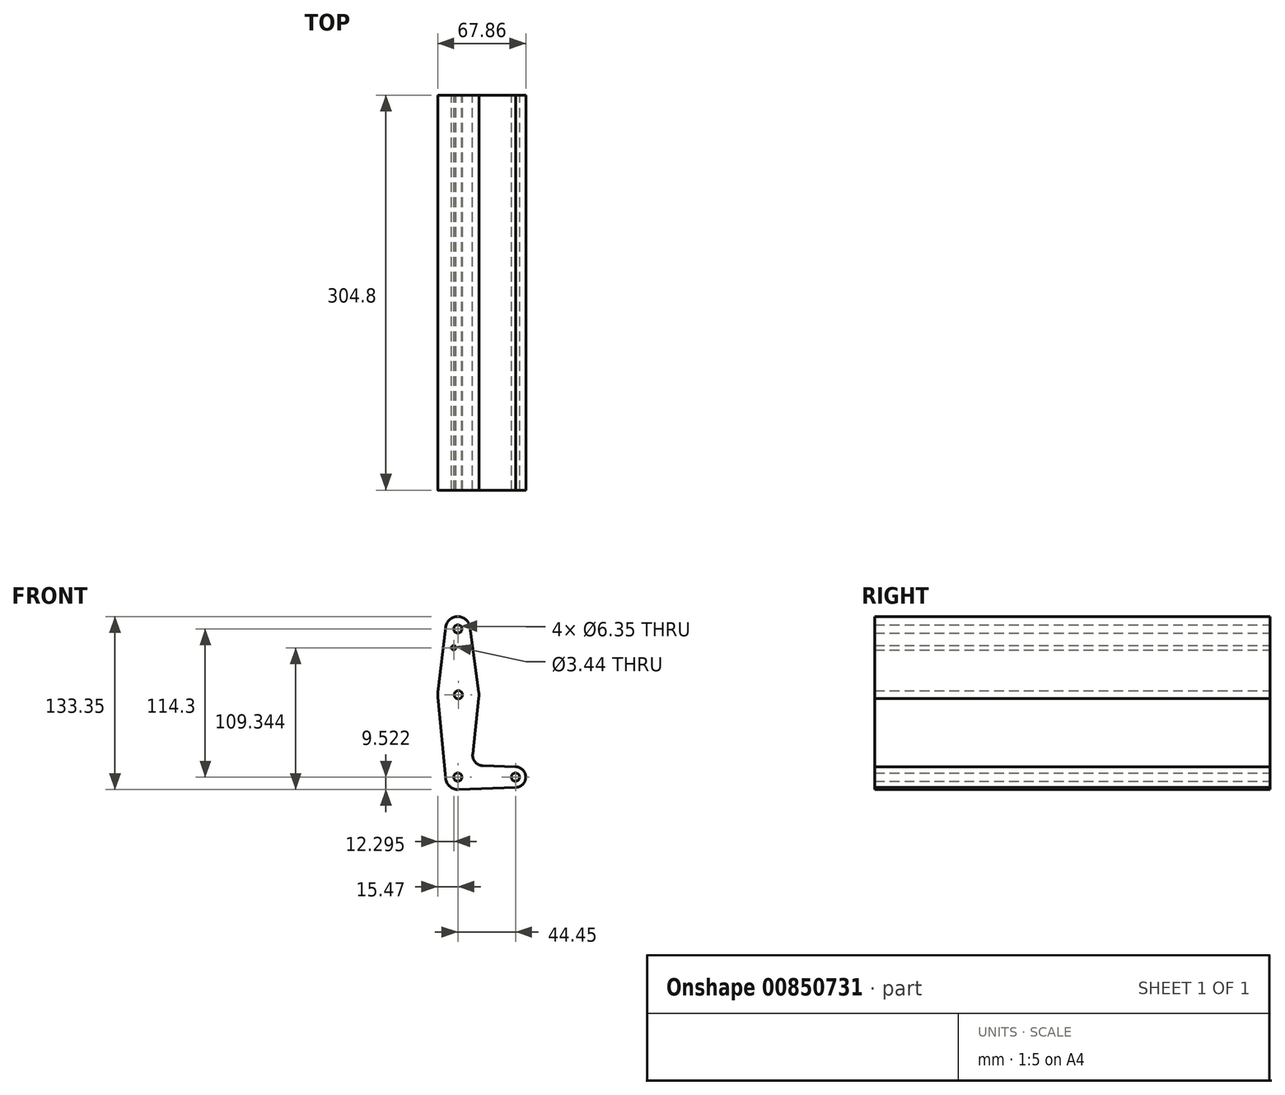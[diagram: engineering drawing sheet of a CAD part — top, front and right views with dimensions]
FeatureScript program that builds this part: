
annotation { "Feature Type Name" : "Feature", "Feature Type Description" : "" }
export const myFeature = defineFeature(function(context is Context, id is Id, definition is map)
    precondition{}
    {
        {
            var Q0;
            Q0=qCreatedBy(makeId("Front.planeOp"),FACE);
            var sketch = newSketch(context, id + "F0", { "sketchPlane" : qUnion([Q0])});
            skCircle(sketch, "E0", {"center": v(-44.45, 103.47) * mm, "radius": 9.53 * mm});
            skCircle(sketch, "E1", {"center": v(-44.05, 52.67) * mm, "radius": 15.88 * mm});
            skCircle(sketch, "E2", {"center": v(-44.45, -10.83) * mm, "radius": 9.53 * mm});
            skCircle(sketch, "E3", {"center": v(0, -10.83) * mm, "radius": 7.94 * mm});
            skLineSegment(sketch, "E4", {"start": v(-44.45, 103.47) * mm, "end": v(-44.45, -10.83) * mm});
            skLineSegment(sketch, "E5", {"start": v(-59.85, 51.18) * mm, "end": v(-53.93, -11.72) * mm});
            skLineSegment(sketch, "E6", {"start": v(-53.9, 104.59) * mm, "end": v(-59.82, 54.53) * mm});
            skLineSegment(sketch, "E7", {"start": v(-35, 104.74) * mm, "end": v(-28.32, 54.78) * mm});
            skCircle(sketch, "E8", {"center": v(-44.45, -10.83) * mm, "radius": 3.18 * mm});
            skCircle(sketch, "E9", {"center": v(-44.05, 52.67) * mm, "radius": 3.18 * mm});
            skCircle(sketch, "E10", {"center": v(-44.45, 103.47) * mm, "radius": 3.18 * mm});
            skCircle(sketch, "E11", {"center": v(0, -10.83) * mm, "radius": 3.18 * mm});
            skCircle(sketch, "E12", {"center": v(-47.63, 89) * mm, "radius": 1.72 * mm});
            skLineSegment(sketch, "E13", {"start": v(-28.41, 49.95) * mm, "end": v(-33, 6.8) * mm});
            skLineSegment(sketch, "E14", {"start": v(0, -10.83) * mm, "end": v(-44.45, -10.83) * mm});
            skLineSegment(sketch, "E15", {"start": v(0, -2.9) * mm, "end": v(-25.38, -1.98) * mm});
            skLineSegment(sketch, "E16", {"start": v(0, -18.77) * mm, "end": v(-44.1, -20.35) * mm});
            skArc(sketch, "E17.filletArc", {"start": v(-33, 6.8) * mm, "mid": v(-31.1, 0.75) * mm, "end": v(-25.38, -1.98) * mm});
            skSolve(sketch);
        }
        {
            var Q0;
            {var subQ10=sQuery(id+"F0.wireOp",EDGE,"E13");Q0=makeQuery(id+"F0.imprint","IMPRINT",FACE,{"disambiguationData":[TD([[makeQuery(id+"F0.imprint","IMPRINT",EDGE,{"derivedFrom":subQ10}),-1.0]])]});}
            var Q1;
            {var subQ0=sQuery(id+"F0.wireOp",EDGE,"E5");Q1=makeQuery(id+"F0.imprint","IMPRINT",FACE,{"disambiguationData":[TD([[makeQuery(id+"F0.imprint","IMPRINT",EDGE,{"derivedFrom":subQ0}),1.0]])]});}
            var Q2;
            {var subQ0=sQuery(id+"F0.wireOp",EDGE,"E2");var subQ8=makeQuery(id+"F0.imprint","INTERSECT",VERTEX,{"derivedFrom":[subQ0,sQuery(id+"F0.wireOp",EDGE,"E5")]});Q2=makeQuery(id+"F0.imprint","IMPRINT",FACE,{"disambiguationData":[TD([[makeQuery(id+"F0.imprint","IMPRINT",EDGE,{"disambiguationData":[TD([[subQ8,1.0]])],"derivedFrom":subQ0}),1.0]])]});}
            var Q3;
            {var subQ0=sQuery(id+"F0.wireOp",EDGE,"E4");var subQ1=sQuery(id+"F0.wireOp",EDGE,"E2");var subQ2=makeQuery(id+"F0.imprint","INTERSECT",VERTEX,{"derivedFrom":[subQ1,subQ0]});Q3=makeQuery(id+"F0.imprint","IMPRINT",FACE,{"disambiguationData":[TD([[makeQuery(id+"F0.imprint","IMPRINT",EDGE,{"disambiguationData":[TD([[subQ2,1.0]])],"derivedFrom":subQ1}),1.0]])]});}
            var Q4;
            {var subQ0=sQuery(id+"F0.wireOp",EDGE,"E16");Q4=makeQuery(id+"F0.imprint","IMPRINT",FACE,{"disambiguationData":[TD([[makeQuery(id+"F0.imprint","IMPRINT",EDGE,{"derivedFrom":subQ0}),-1.0]])]});}
            var Q5;
            Q5=makeQuery(id+"F0.imprint","IMPRINT",FACE,{"disambiguationData":[TD([[makeQuery(id+"F0.imprint","IMPRINT",EDGE,{"derivedFrom":sQuery(id+"F0.wireOp",EDGE,"E11")}),-1.0]])]});
            var Q6;
            {var subQ1=sQuery(id+"F0.wireOp",EDGE,"E1");var subQ8=makeQuery(id+"F0.imprint","INTERSECT",VERTEX,{"derivedFrom":[subQ1,sQuery(id+"F0.wireOp",EDGE,"E7")]});Q6=makeQuery(id+"F0.imprint","IMPRINT",FACE,{"disambiguationData":[TD([[makeQuery(id+"F0.imprint","IMPRINT",EDGE,{"disambiguationData":[TD([[subQ8,-1.0]])],"derivedFrom":subQ1}),1.0]])]});}
            var Q7;
            {var subQ1=sQuery(id+"F0.wireOp",EDGE,"E1");var subQ8=makeQuery(id+"F0.imprint","INTERSECT",VERTEX,{"derivedFrom":[subQ1,sQuery(id+"F0.wireOp",EDGE,"E6")]});Q7=makeQuery(id+"F0.imprint","IMPRINT",FACE,{"disambiguationData":[TD([[makeQuery(id+"F0.imprint","IMPRINT",EDGE,{"disambiguationData":[TD([[subQ8,1.0]])],"derivedFrom":subQ1}),1.0]])]});}
            var Q8;
            {var subQ0=sQuery(id+"F0.wireOp",EDGE,"E6");Q8=makeQuery(id+"F0.imprint","IMPRINT",FACE,{"disambiguationData":[TD([[makeQuery(id+"F0.imprint","IMPRINT",EDGE,{"derivedFrom":subQ0}),1.0]])]});}
            var Q9;
            {var subQ0=sQuery(id+"F0.wireOp",EDGE,"E7");Q9=makeQuery(id+"F0.imprint","IMPRINT",FACE,{"disambiguationData":[TD([[makeQuery(id+"F0.imprint","IMPRINT",EDGE,{"derivedFrom":subQ0}),-1.0]])]});}
            var Q10;
            Q10=makeQuery(id+"F0.imprint","IMPRINT",FACE,{"disambiguationData":[TD([[makeQuery(id+"F0.imprint","IMPRINT",EDGE,{"derivedFrom":sQuery(id+"F0.wireOp",EDGE,"E10")}),-1.0]])]});
            extrude(context, id + "F1", {"entities" : qUnion([Q0, Q1, Q2, Q3, Q4, Q5, Q6, Q7, Q8, Q9, Q10]), "depth" : 304.8 * mm, "offsetDistance" : 25.4 * mm});
        }
    });
